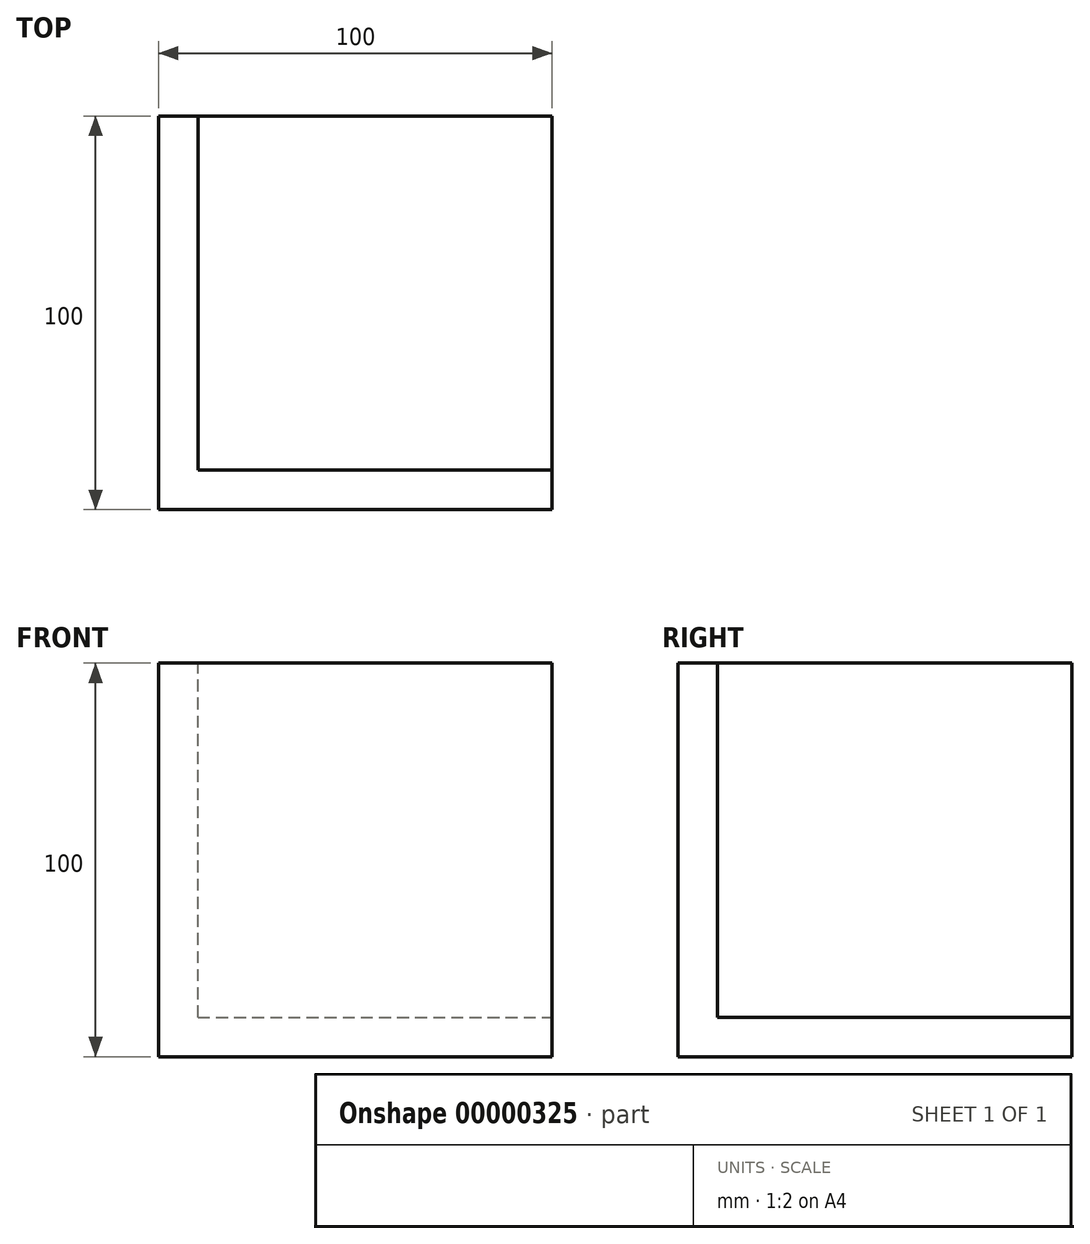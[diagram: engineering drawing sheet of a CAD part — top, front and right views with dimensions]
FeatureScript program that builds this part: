
annotation { "Feature Type Name" : "Feature", "Feature Type Description" : "" }
export const myFeature = defineFeature(function(context is Context, id is Id, definition is map)
    precondition{}
    {
        {
            var Q0;
            Q0=qCreatedBy(makeId("Front.planeOp"),FACE);
            var sketch = newSketch(context, id + "F0", { "sketchPlane" : qUnion([Q0])});
            skLineSegment(sketch, "E0.bottom", {"start": v(0, 0) * mm, "end": v(100, 0) * mm});
            skLineSegment(sketch, "E0.top", {"start": v(0, 100) * mm, "end": v(100, 100) * mm});
            skLineSegment(sketch, "E0.left", {"start": v(0, 0) * mm, "end": v(0, 100) * mm});
            skLineSegment(sketch, "E0.right", {"start": v(100, 0) * mm, "end": v(100, 100) * mm});
            skSolve(sketch);
        }
        {
            var Q0;
            Q0=makeQuery(id+"F0.imprint","IMPRINT",FACE,{"disambiguationData":[TD([[makeQuery(id+"F0.imprint","IMPRINT",EDGE,{"derivedFrom":sQuery(id+"F0.wireOp",EDGE,"E0.bottom")}),1.0]])]});
            extrude(context, id + "F1", {"entities" : qUnion([Q0]), "oppositeDirection" : true, "depth" : 100 * mm});
        }
        {
            var Q0;
            Q0=makeQuery(id+"F1.opExtrude","SWEPT_FACE",FACE,{"disambiguationData":[OSD([sQuery(id+"F0.wireOp",EDGE,"E0.top")])]});
            var Q1;
            Q1=makeQuery(id+"F1.opExtrude","SWEPT_FACE",FACE,{"disambiguationData":[OSD([sQuery(id+"F0.wireOp",EDGE,"E0.right")])]});
            var Q2;
            Q2=makeQuery(id+"F1.opExtrude","CAP_FACE",FACE,{"disambiguationData":[OSD([sQuery(id+"F0.wireOp",EDGE,"E0.bottom"),sQuery(id+"F0.wireOp",EDGE,"E0.top"),sQuery(id+"F0.wireOp",EDGE,"E0.left"),sQuery(id+"F0.wireOp",EDGE,"E0.right")])],"isStart":false});
            shell(context, id + "F2", {"entities" : qUnion([Q0, Q1, Q2]), "thickness" : 10 * mm});
        }
    });
